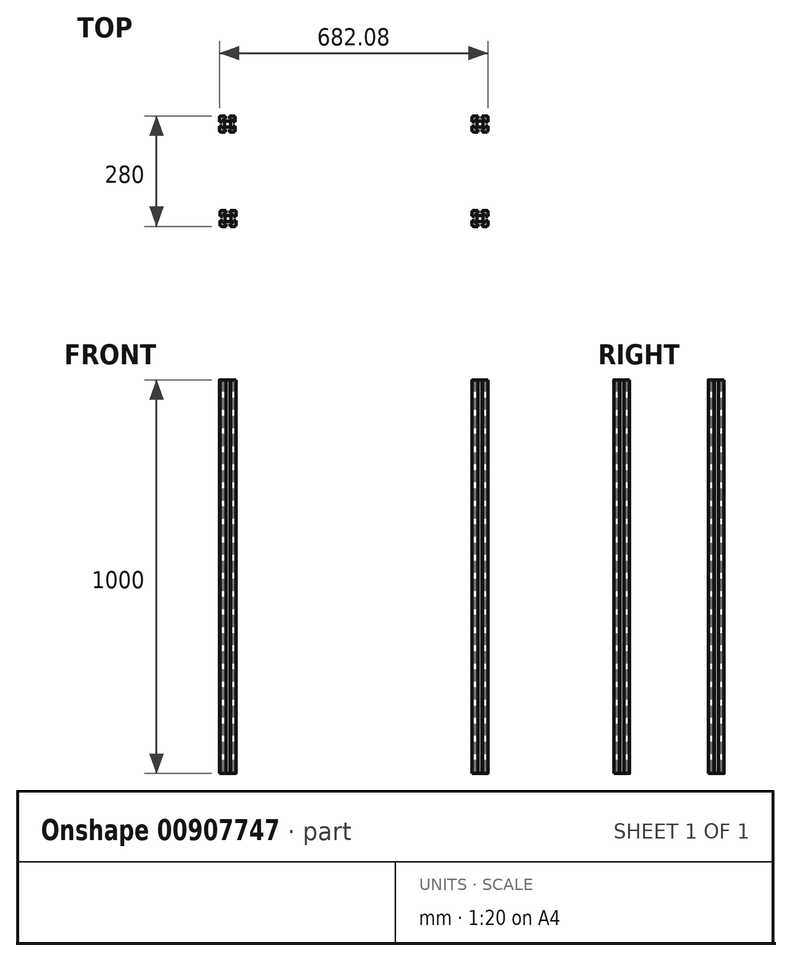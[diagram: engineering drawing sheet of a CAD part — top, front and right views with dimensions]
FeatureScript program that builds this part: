
annotation { "Feature Type Name" : "Feature", "Feature Type Description" : "" }
export const myFeature = defineFeature(function(context is Context, id is Id, definition is map)
    precondition{}
    {
        {
            var Q0;
            Q0=qCreatedBy(makeId("Top.planeOp"),FACE);
            var sketch = newSketch(context, id + "F0", { "sketchPlane" : qUnion([Q0])});
            skLineSegment(sketch, "E0", {"start": v(5.8, -18.5) * mm, "end": v(5.8, -20) * mm});
            skLineSegment(sketch, "E1", {"start": v(5.8, -20) * mm, "end": v(17, -20) * mm});
            skArc(sketch, "E2", {"start": v(17, -20) * mm, "mid": v(19.12, -19.12) * mm, "end": v(20, -17) * mm});
            skLineSegment(sketch, "E3", {"start": v(20, -17) * mm, "end": v(20, -5.8) * mm});
            skLineSegment(sketch, "E4", {"start": v(20, -5.8) * mm, "end": v(18.5, -5.8) * mm});
            skLineSegment(sketch, "E5", {"start": v(18.5, -5.8) * mm, "end": v(18.5, -5) * mm});
            skLineSegment(sketch, "E6", {"start": v(18.5, -5) * mm, "end": v(14, -5) * mm});
            skLineSegment(sketch, "E7", {"start": v(14, -5) * mm, "end": v(14, -10.05) * mm});
            skLineSegment(sketch, "E8", {"start": v(14, -10.05) * mm, "end": v(11.46, -10.05) * mm});
            skLineSegment(sketch, "E9", {"start": v(11.46, -10.05) * mm, "end": v(7.5, -6.09) * mm});
            skLineSegment(sketch, "E10", {"start": v(7.5, -6.09) * mm, "end": v(7.5, 6.09) * mm});
            skLineSegment(sketch, "E11", {"start": v(7.5, 6.09) * mm, "end": v(11.46, 10.05) * mm});
            skLineSegment(sketch, "E12", {"start": v(11.46, 10.05) * mm, "end": v(14, 10.05) * mm});
            skLineSegment(sketch, "E13", {"start": v(14, 10.05) * mm, "end": v(14, 5) * mm});
            skLineSegment(sketch, "E14", {"start": v(14, 5) * mm, "end": v(18.5, 5) * mm});
            skLineSegment(sketch, "E15", {"start": v(18.5, 5) * mm, "end": v(18.5, 5.8) * mm});
            skLineSegment(sketch, "E16", {"start": v(18.5, 5.8) * mm, "end": v(20, 5.8) * mm});
            skLineSegment(sketch, "E17", {"start": v(20, 5.8) * mm, "end": v(20, 17) * mm});
            skArc(sketch, "E18", {"start": v(20, 17) * mm, "mid": v(19.12, 19.12) * mm, "end": v(17, 20) * mm});
            skLineSegment(sketch, "E19", {"start": v(17, 20) * mm, "end": v(5.8, 20) * mm});
            skLineSegment(sketch, "E20", {"start": v(5.8, 20) * mm, "end": v(5.8, 18.5) * mm});
            skLineSegment(sketch, "E21", {"start": v(5.8, 18.5) * mm, "end": v(5, 18.5) * mm});
            skLineSegment(sketch, "E22", {"start": v(5, 18.5) * mm, "end": v(5, 14) * mm});
            skLineSegment(sketch, "E23", {"start": v(5, 14) * mm, "end": v(10.05, 14) * mm});
            skLineSegment(sketch, "E24", {"start": v(10.05, 14) * mm, "end": v(10.05, 11.46) * mm});
            skLineSegment(sketch, "E25", {"start": v(10.05, 11.46) * mm, "end": v(6.09, 7.5) * mm});
            skLineSegment(sketch, "E26", {"start": v(6.09, 7.5) * mm, "end": v(-6.09, 7.5) * mm});
            skLineSegment(sketch, "E27", {"start": v(-6.09, 7.5) * mm, "end": v(-10.05, 11.46) * mm});
            skLineSegment(sketch, "E28", {"start": v(-10.05, 11.46) * mm, "end": v(-10.05, 14) * mm});
            skLineSegment(sketch, "E29", {"start": v(-10.05, 14) * mm, "end": v(-5, 14) * mm});
            skLineSegment(sketch, "E30", {"start": v(-5, 14) * mm, "end": v(-5, 18.5) * mm});
            skLineSegment(sketch, "E31", {"start": v(-5, 18.5) * mm, "end": v(-5.8, 18.5) * mm});
            skLineSegment(sketch, "E32", {"start": v(-5.8, 18.5) * mm, "end": v(-5.8, 20) * mm});
            skLineSegment(sketch, "E33", {"start": v(-5.8, 20) * mm, "end": v(-17, 20) * mm});
            skArc(sketch, "E34", {"start": v(-17, 20) * mm, "mid": v(-19.12, 19.12) * mm, "end": v(-20, 17) * mm});
            skLineSegment(sketch, "E35", {"start": v(-20, 17) * mm, "end": v(-20, 5.8) * mm});
            skLineSegment(sketch, "E36", {"start": v(-20, 5.8) * mm, "end": v(-18.5, 5.8) * mm});
            skLineSegment(sketch, "E37", {"start": v(-18.5, 5.8) * mm, "end": v(-18.5, 5) * mm});
            skLineSegment(sketch, "E38", {"start": v(-18.5, 5) * mm, "end": v(-14, 5) * mm});
            skLineSegment(sketch, "E39", {"start": v(-14, 5) * mm, "end": v(-14, 10.05) * mm});
            skLineSegment(sketch, "E40", {"start": v(-14, 10.05) * mm, "end": v(-11.46, 10.05) * mm});
            skLineSegment(sketch, "E41", {"start": v(-11.46, 10.05) * mm, "end": v(-7.5, 6.09) * mm});
            skLineSegment(sketch, "E42", {"start": v(-7.5, 6.09) * mm, "end": v(-7.5, -6.09) * mm});
            skLineSegment(sketch, "E43", {"start": v(-7.5, -6.09) * mm, "end": v(-11.46, -10.05) * mm});
            skLineSegment(sketch, "E44", {"start": v(-11.46, -10.05) * mm, "end": v(-14, -10.05) * mm});
            skLineSegment(sketch, "E45", {"start": v(-14, -10.05) * mm, "end": v(-14, -5) * mm});
            skLineSegment(sketch, "E46", {"start": v(-14, -5) * mm, "end": v(-18.5, -5) * mm});
            skLineSegment(sketch, "E47", {"start": v(-18.5, -5) * mm, "end": v(-18.5, -5.8) * mm});
            skLineSegment(sketch, "E48", {"start": v(-18.5, -5.8) * mm, "end": v(-20, -5.8) * mm});
            skLineSegment(sketch, "E49", {"start": v(-20, -5.8) * mm, "end": v(-20, -17) * mm});
            skArc(sketch, "E50", {"start": v(-20, -17) * mm, "mid": v(-19.12, -19.12) * mm, "end": v(-17, -20) * mm});
            skLineSegment(sketch, "E51", {"start": v(-17, -20) * mm, "end": v(-5.8, -20) * mm});
            skLineSegment(sketch, "E52", {"start": v(-5.8, -20) * mm, "end": v(-5.8, -18.5) * mm});
            skLineSegment(sketch, "E53", {"start": v(-5.8, -18.5) * mm, "end": v(-5, -18.5) * mm});
            skLineSegment(sketch, "E54", {"start": v(-5, -18.5) * mm, "end": v(-5, -14) * mm});
            skLineSegment(sketch, "E55", {"start": v(-5, -14) * mm, "end": v(-10.05, -14) * mm});
            skLineSegment(sketch, "E56", {"start": v(-10.05, -14) * mm, "end": v(-10.05, -11.46) * mm});
            skLineSegment(sketch, "E57", {"start": v(-10.05, -11.46) * mm, "end": v(-6.09, -7.5) * mm});
            skLineSegment(sketch, "E58", {"start": v(-6.09, -7.5) * mm, "end": v(6.09, -7.5) * mm});
            skLineSegment(sketch, "E59", {"start": v(6.09, -7.5) * mm, "end": v(10.05, -11.46) * mm});
            skLineSegment(sketch, "E60", {"start": v(10.05, -11.46) * mm, "end": v(10.05, -14) * mm});
            skLineSegment(sketch, "E61", {"start": v(10.05, -14) * mm, "end": v(5, -14) * mm});
            skLineSegment(sketch, "E62", {"start": v(5, -14) * mm, "end": v(5, -18.5) * mm});
            skLineSegment(sketch, "E63", {"start": v(5, -18.5) * mm, "end": v(5.8, -18.5) * mm});
            skLineSegment(sketch, "E64", {"start": v(18.5, 9.5) * mm, "end": v(18.5, 14.5) * mm});
            skArc(sketch, "E65", {"start": v(15.5, 9.5) * mm, "mid": v(17, 8) * mm, "end": v(18.5, 9.5) * mm});
            skLineSegment(sketch, "E66", {"start": v(15.5, 11.75) * mm, "end": v(15.5, 9.5) * mm});
            skLineSegment(sketch, "E67", {"start": v(14.5, 11.75) * mm, "end": v(15.5, 11.75) * mm});
            skArc(sketch, "E68", {"start": v(11.75, 14.5) * mm, "mid": v(12.56, 12.56) * mm, "end": v(14.5, 11.75) * mm});
            skLineSegment(sketch, "E69", {"start": v(11.75, 15.5) * mm, "end": v(11.75, 14.5) * mm});
            skLineSegment(sketch, "E70", {"start": v(9.5, 15.5) * mm, "end": v(11.75, 15.5) * mm});
            skArc(sketch, "E71", {"start": v(9.5, 18.5) * mm, "mid": v(8, 17) * mm, "end": v(9.5, 15.5) * mm});
            skLineSegment(sketch, "E72", {"start": v(14.5, 18.5) * mm, "end": v(9.5, 18.5) * mm});
            skLineSegment(sketch, "E73", {"start": v(14.5, 17.25) * mm, "end": v(14.5, 18.5) * mm});
            skArc(sketch, "E74", {"start": v(17.25, 14.5) * mm, "mid": v(16.44, 16.44) * mm, "end": v(14.5, 17.25) * mm});
            skLineSegment(sketch, "E75", {"start": v(18.5, 14.5) * mm, "end": v(17.25, 14.5) * mm});
            skLineSegment(sketch, "E76", {"start": v(11.75, -14.5) * mm, "end": v(11.75, -15.5) * mm});
            skArc(sketch, "E77", {"start": v(14.5, -11.75) * mm, "mid": v(12.56, -12.56) * mm, "end": v(11.75, -14.5) * mm});
            skLineSegment(sketch, "E78", {"start": v(15.5, -11.75) * mm, "end": v(14.5, -11.75) * mm});
            skLineSegment(sketch, "E79", {"start": v(15.5, -9.5) * mm, "end": v(15.5, -11.75) * mm});
            skArc(sketch, "E80", {"start": v(18.5, -9.5) * mm, "mid": v(17, -8) * mm, "end": v(15.5, -9.5) * mm});
            skLineSegment(sketch, "E81", {"start": v(18.5, -14.5) * mm, "end": v(18.5, -9.5) * mm});
            skLineSegment(sketch, "E82", {"start": v(17.25, -14.5) * mm, "end": v(18.5, -14.5) * mm});
            skArc(sketch, "E83", {"start": v(14.5, -17.25) * mm, "mid": v(16.44, -16.44) * mm, "end": v(17.25, -14.5) * mm});
            skLineSegment(sketch, "E84", {"start": v(14.5, -18.5) * mm, "end": v(14.5, -17.25) * mm});
            skLineSegment(sketch, "E85", {"start": v(9.5, -18.5) * mm, "end": v(14.5, -18.5) * mm});
            skArc(sketch, "E86", {"start": v(9.5, -15.5) * mm, "mid": v(8, -17) * mm, "end": v(9.5, -18.5) * mm});
            skLineSegment(sketch, "E87", {"start": v(11.75, -15.5) * mm, "end": v(9.5, -15.5) * mm});
            skLineSegment(sketch, "E88", {"start": v(-2, 4.58) * mm, "end": v(-2.4, 5.5) * mm});
            skArc(sketch, "E89", {"start": v(2, 4.58) * mm, "mid": v(0, 5) * mm, "end": v(-2, 4.58) * mm});
            skLineSegment(sketch, "E90", {"start": v(2.4, 5.5) * mm, "end": v(2, 4.58) * mm});
            skLineSegment(sketch, "E91", {"start": v(5.5, 5.5) * mm, "end": v(2.4, 5.5) * mm});
            skLineSegment(sketch, "E92", {"start": v(5.5, 2.4) * mm, "end": v(5.5, 5.5) * mm});
            skLineSegment(sketch, "E93", {"start": v(4.58, 2) * mm, "end": v(5.5, 2.4) * mm});
            skArc(sketch, "E94", {"start": v(4.58, -2) * mm, "mid": v(5, 0) * mm, "end": v(4.58, 2) * mm});
            skLineSegment(sketch, "E95", {"start": v(5.5, -2.4) * mm, "end": v(4.58, -2) * mm});
            skLineSegment(sketch, "E96", {"start": v(5.5, -5.5) * mm, "end": v(5.5, -2.4) * mm});
            skLineSegment(sketch, "E97", {"start": v(2.4, -5.5) * mm, "end": v(5.5, -5.5) * mm});
            skLineSegment(sketch, "E98", {"start": v(2, -4.58) * mm, "end": v(2.4, -5.5) * mm});
            skArc(sketch, "E99", {"start": v(-2, -4.58) * mm, "mid": v(0, -5) * mm, "end": v(2, -4.58) * mm});
            skLineSegment(sketch, "E100", {"start": v(-2.4, -5.5) * mm, "end": v(-2, -4.58) * mm});
            skLineSegment(sketch, "E101", {"start": v(-5.5, -5.5) * mm, "end": v(-2.4, -5.5) * mm});
            skLineSegment(sketch, "E102", {"start": v(-5.5, -2.4) * mm, "end": v(-5.5, -5.5) * mm});
            skLineSegment(sketch, "E103", {"start": v(-4.58, -2) * mm, "end": v(-5.5, -2.4) * mm});
            skArc(sketch, "E104", {"start": v(-4.58, 2) * mm, "mid": v(-5, 0) * mm, "end": v(-4.58, -2) * mm});
            skLineSegment(sketch, "E105", {"start": v(-5.5, 2.4) * mm, "end": v(-4.58, 2) * mm});
            skLineSegment(sketch, "E106", {"start": v(-5.5, 5.5) * mm, "end": v(-5.5, 2.4) * mm});
            skLineSegment(sketch, "E107", {"start": v(-2.4, 5.5) * mm, "end": v(-5.5, 5.5) * mm});
            skLineSegment(sketch, "E108", {"start": v(-18.5, -9.5) * mm, "end": v(-18.5, -14.5) * mm});
            skArc(sketch, "E109", {"start": v(-15.5, -9.5) * mm, "mid": v(-17, -8) * mm, "end": v(-18.5, -9.5) * mm});
            skLineSegment(sketch, "E110", {"start": v(-15.5, -11.75) * mm, "end": v(-15.5, -9.5) * mm});
            skLineSegment(sketch, "E111", {"start": v(-14.5, -11.75) * mm, "end": v(-15.5, -11.75) * mm});
            skArc(sketch, "E112", {"start": v(-11.75, -14.5) * mm, "mid": v(-12.56, -12.56) * mm, "end": v(-14.5, -11.75) * mm});
            skLineSegment(sketch, "E113", {"start": v(-11.75, -15.5) * mm, "end": v(-11.75, -14.5) * mm});
            skLineSegment(sketch, "E114", {"start": v(-9.5, -15.5) * mm, "end": v(-11.75, -15.5) * mm});
            skArc(sketch, "E115", {"start": v(-9.5, -18.5) * mm, "mid": v(-8, -17) * mm, "end": v(-9.5, -15.5) * mm});
            skLineSegment(sketch, "E116", {"start": v(-14.5, -18.5) * mm, "end": v(-9.5, -18.5) * mm});
            skLineSegment(sketch, "E117", {"start": v(-14.5, -17.25) * mm, "end": v(-14.5, -18.5) * mm});
            skArc(sketch, "E118", {"start": v(-17.25, -14.5) * mm, "mid": v(-16.44, -16.44) * mm, "end": v(-14.5, -17.25) * mm});
            skLineSegment(sketch, "E119", {"start": v(-18.5, -14.5) * mm, "end": v(-17.25, -14.5) * mm});
            skLineSegment(sketch, "E120", {"start": v(-11.75, 14.5) * mm, "end": v(-11.75, 15.5) * mm});
            skArc(sketch, "E121", {"start": v(-14.5, 11.75) * mm, "mid": v(-12.56, 12.56) * mm, "end": v(-11.75, 14.5) * mm});
            skLineSegment(sketch, "E122", {"start": v(-15.5, 11.75) * mm, "end": v(-14.5, 11.75) * mm});
            skLineSegment(sketch, "E123", {"start": v(-15.5, 9.5) * mm, "end": v(-15.5, 11.75) * mm});
            skArc(sketch, "E124", {"start": v(-18.5, 9.5) * mm, "mid": v(-17, 8) * mm, "end": v(-15.5, 9.5) * mm});
            skLineSegment(sketch, "E125", {"start": v(-18.5, 14.5) * mm, "end": v(-18.5, 9.5) * mm});
            skLineSegment(sketch, "E126", {"start": v(-17.25, 14.5) * mm, "end": v(-18.5, 14.5) * mm});
            skArc(sketch, "E127", {"start": v(-14.5, 17.25) * mm, "mid": v(-16.44, 16.44) * mm, "end": v(-17.25, 14.5) * mm});
            skLineSegment(sketch, "E128", {"start": v(-14.5, 18.5) * mm, "end": v(-14.5, 17.25) * mm});
            skLineSegment(sketch, "E129", {"start": v(-9.5, 18.5) * mm, "end": v(-14.5, 18.5) * mm});
            skArc(sketch, "E130", {"start": v(-9.5, 15.5) * mm, "mid": v(-8, 17) * mm, "end": v(-9.5, 18.5) * mm});
            skLineSegment(sketch, "E131", {"start": v(-11.75, 15.5) * mm, "end": v(-9.5, 15.5) * mm});
            skLineSegment(sketch, "E132", {"start": v(645.88, -18.5) * mm, "end": v(645.88, -20) * mm});
            skLineSegment(sketch, "E133", {"start": v(645.88, -20) * mm, "end": v(657.08, -20) * mm});
            skArc(sketch, "E134", {"start": v(657.08, -20) * mm, "mid": v(659.2, -19.12) * mm, "end": v(660.08, -17) * mm});
            skLineSegment(sketch, "E135", {"start": v(660.08, -17) * mm, "end": v(660.08, -5.8) * mm});
            skLineSegment(sketch, "E136", {"start": v(660.08, -5.8) * mm, "end": v(658.58, -5.8) * mm});
            skLineSegment(sketch, "E137", {"start": v(658.58, -5.8) * mm, "end": v(658.58, -5) * mm});
            skLineSegment(sketch, "E138", {"start": v(658.58, -5) * mm, "end": v(654.08, -5) * mm});
            skLineSegment(sketch, "E139", {"start": v(654.08, -5) * mm, "end": v(654.08, -10.05) * mm});
            skLineSegment(sketch, "E140", {"start": v(654.08, -10.05) * mm, "end": v(651.54, -10.05) * mm});
            skLineSegment(sketch, "E141", {"start": v(651.54, -10.05) * mm, "end": v(647.58, -6.09) * mm});
            skLineSegment(sketch, "E142", {"start": v(647.58, -6.09) * mm, "end": v(647.58, 6.09) * mm});
            skLineSegment(sketch, "E143", {"start": v(647.58, 6.09) * mm, "end": v(651.54, 10.05) * mm});
            skLineSegment(sketch, "E144", {"start": v(651.54, 10.05) * mm, "end": v(654.08, 10.05) * mm});
            skLineSegment(sketch, "E145", {"start": v(654.08, 10.05) * mm, "end": v(654.08, 5) * mm});
            skLineSegment(sketch, "E146", {"start": v(654.08, 5) * mm, "end": v(658.58, 5) * mm});
            skLineSegment(sketch, "E147", {"start": v(658.58, 5) * mm, "end": v(658.58, 5.8) * mm});
            skLineSegment(sketch, "E148", {"start": v(658.58, 5.8) * mm, "end": v(660.08, 5.8) * mm});
            skLineSegment(sketch, "E149", {"start": v(660.08, 5.8) * mm, "end": v(660.08, 17) * mm});
            skArc(sketch, "E150", {"start": v(660.08, 17) * mm, "mid": v(659.2, 19.12) * mm, "end": v(657.08, 20) * mm});
            skLineSegment(sketch, "E151", {"start": v(657.08, 20) * mm, "end": v(645.88, 20) * mm});
            skLineSegment(sketch, "E152", {"start": v(645.88, 20) * mm, "end": v(645.88, 18.5) * mm});
            skLineSegment(sketch, "E153", {"start": v(645.88, 18.5) * mm, "end": v(645.08, 18.5) * mm});
            skLineSegment(sketch, "E154", {"start": v(645.08, 18.5) * mm, "end": v(645.08, 14) * mm});
            skLineSegment(sketch, "E155", {"start": v(645.08, 14) * mm, "end": v(650.13, 14) * mm});
            skLineSegment(sketch, "E156", {"start": v(650.13, 14) * mm, "end": v(650.13, 11.46) * mm});
            skLineSegment(sketch, "E157", {"start": v(650.13, 11.46) * mm, "end": v(646.16, 7.5) * mm});
            skLineSegment(sketch, "E158", {"start": v(646.16, 7.5) * mm, "end": v(634, 7.5) * mm});
            skLineSegment(sketch, "E159", {"start": v(634, 7.5) * mm, "end": v(630.03, 11.46) * mm});
            skLineSegment(sketch, "E160", {"start": v(630.03, 11.46) * mm, "end": v(630.03, 14) * mm});
            skLineSegment(sketch, "E161", {"start": v(630.03, 14) * mm, "end": v(635.08, 14) * mm});
            skLineSegment(sketch, "E162", {"start": v(635.08, 14) * mm, "end": v(635.08, 18.5) * mm});
            skLineSegment(sketch, "E163", {"start": v(635.08, 18.5) * mm, "end": v(634.28, 18.5) * mm});
            skLineSegment(sketch, "E164", {"start": v(634.28, 18.5) * mm, "end": v(634.28, 20) * mm});
            skLineSegment(sketch, "E165", {"start": v(634.28, 20) * mm, "end": v(623.08, 20) * mm});
            skArc(sketch, "E166", {"start": v(623.08, 20) * mm, "mid": v(620.96, 19.12) * mm, "end": v(620.08, 17) * mm});
            skLineSegment(sketch, "E167", {"start": v(620.08, 17) * mm, "end": v(620.08, 5.8) * mm});
            skLineSegment(sketch, "E168", {"start": v(620.08, 5.8) * mm, "end": v(621.58, 5.8) * mm});
            skLineSegment(sketch, "E169", {"start": v(621.58, 5.8) * mm, "end": v(621.58, 5) * mm});
            skLineSegment(sketch, "E170", {"start": v(621.58, 5) * mm, "end": v(626.08, 5) * mm});
            skLineSegment(sketch, "E171", {"start": v(626.08, 5) * mm, "end": v(626.08, 10.05) * mm});
            skLineSegment(sketch, "E172", {"start": v(626.08, 10.05) * mm, "end": v(628.61, 10.05) * mm});
            skLineSegment(sketch, "E173", {"start": v(628.61, 10.05) * mm, "end": v(632.58, 6.09) * mm});
            skLineSegment(sketch, "E174", {"start": v(632.58, 6.09) * mm, "end": v(632.58, -6.09) * mm});
            skLineSegment(sketch, "E175", {"start": v(632.58, -6.09) * mm, "end": v(628.61, -10.05) * mm});
            skLineSegment(sketch, "E176", {"start": v(628.61, -10.05) * mm, "end": v(626.08, -10.05) * mm});
            skLineSegment(sketch, "E177", {"start": v(626.08, -10.05) * mm, "end": v(626.08, -5) * mm});
            skLineSegment(sketch, "E178", {"start": v(626.08, -5) * mm, "end": v(621.58, -5) * mm});
            skLineSegment(sketch, "E179", {"start": v(621.58, -5) * mm, "end": v(621.58, -5.8) * mm});
            skLineSegment(sketch, "E180", {"start": v(621.58, -5.8) * mm, "end": v(620.08, -5.8) * mm});
            skLineSegment(sketch, "E181", {"start": v(620.08, -5.8) * mm, "end": v(620.08, -17) * mm});
            skArc(sketch, "E182", {"start": v(620.08, -17) * mm, "mid": v(620.96, -19.12) * mm, "end": v(623.08, -20) * mm});
            skLineSegment(sketch, "E183", {"start": v(623.08, -20) * mm, "end": v(634.28, -20) * mm});
            skLineSegment(sketch, "E184", {"start": v(634.28, -20) * mm, "end": v(634.28, -18.5) * mm});
            skLineSegment(sketch, "E185", {"start": v(634.28, -18.5) * mm, "end": v(635.08, -18.5) * mm});
            skLineSegment(sketch, "E186", {"start": v(635.08, -18.5) * mm, "end": v(635.08, -14) * mm});
            skLineSegment(sketch, "E187", {"start": v(635.08, -14) * mm, "end": v(630.03, -14) * mm});
            skLineSegment(sketch, "E188", {"start": v(630.03, -14) * mm, "end": v(630.03, -11.46) * mm});
            skLineSegment(sketch, "E189", {"start": v(630.03, -11.46) * mm, "end": v(634, -7.5) * mm});
            skLineSegment(sketch, "E190", {"start": v(634, -7.5) * mm, "end": v(646.16, -7.5) * mm});
            skLineSegment(sketch, "E191", {"start": v(646.16, -7.5) * mm, "end": v(650.13, -11.46) * mm});
            skLineSegment(sketch, "E192", {"start": v(650.13, -11.46) * mm, "end": v(650.13, -14) * mm});
            skLineSegment(sketch, "E193", {"start": v(650.13, -14) * mm, "end": v(645.08, -14) * mm});
            skLineSegment(sketch, "E194", {"start": v(645.08, -14) * mm, "end": v(645.08, -18.5) * mm});
            skLineSegment(sketch, "E195", {"start": v(645.08, -18.5) * mm, "end": v(645.88, -18.5) * mm});
            skLineSegment(sketch, "E196", {"start": v(658.58, 9.5) * mm, "end": v(658.58, 14.5) * mm});
            skArc(sketch, "E197", {"start": v(655.58, 9.5) * mm, "mid": v(657.08, 8) * mm, "end": v(658.58, 9.5) * mm});
            skLineSegment(sketch, "E198", {"start": v(655.58, 11.75) * mm, "end": v(655.58, 9.5) * mm});
            skLineSegment(sketch, "E199", {"start": v(654.58, 11.75) * mm, "end": v(655.58, 11.75) * mm});
            skArc(sketch, "E200", {"start": v(651.83, 14.5) * mm, "mid": v(652.63, 12.56) * mm, "end": v(654.58, 11.75) * mm});
            skLineSegment(sketch, "E201", {"start": v(651.83, 15.5) * mm, "end": v(651.83, 14.5) * mm});
            skLineSegment(sketch, "E202", {"start": v(649.58, 15.5) * mm, "end": v(651.83, 15.5) * mm});
            skArc(sketch, "E203", {"start": v(649.58, 18.5) * mm, "mid": v(648.08, 17) * mm, "end": v(649.58, 15.5) * mm});
            skLineSegment(sketch, "E204", {"start": v(654.58, 18.5) * mm, "end": v(649.58, 18.5) * mm});
            skLineSegment(sketch, "E205", {"start": v(654.58, 17.25) * mm, "end": v(654.58, 18.5) * mm});
            skArc(sketch, "E206", {"start": v(657.33, 14.5) * mm, "mid": v(656.52, 16.44) * mm, "end": v(654.58, 17.25) * mm});
            skLineSegment(sketch, "E207", {"start": v(658.58, 14.5) * mm, "end": v(657.33, 14.5) * mm});
            skLineSegment(sketch, "E208", {"start": v(651.83, -14.5) * mm, "end": v(651.83, -15.5) * mm});
            skArc(sketch, "E209", {"start": v(654.58, -11.75) * mm, "mid": v(652.63, -12.56) * mm, "end": v(651.83, -14.5) * mm});
            skLineSegment(sketch, "E210", {"start": v(655.58, -11.75) * mm, "end": v(654.58, -11.75) * mm});
            skLineSegment(sketch, "E211", {"start": v(655.58, -9.5) * mm, "end": v(655.58, -11.75) * mm});
            skArc(sketch, "E212", {"start": v(658.58, -9.5) * mm, "mid": v(657.08, -8) * mm, "end": v(655.58, -9.5) * mm});
            skLineSegment(sketch, "E213", {"start": v(658.58, -14.5) * mm, "end": v(658.58, -9.5) * mm});
            skLineSegment(sketch, "E214", {"start": v(657.33, -14.5) * mm, "end": v(658.58, -14.5) * mm});
            skArc(sketch, "E215", {"start": v(654.58, -17.25) * mm, "mid": v(656.52, -16.44) * mm, "end": v(657.33, -14.5) * mm});
            skLineSegment(sketch, "E216", {"start": v(654.58, -18.5) * mm, "end": v(654.58, -17.25) * mm});
            skLineSegment(sketch, "E217", {"start": v(649.58, -18.5) * mm, "end": v(654.58, -18.5) * mm});
            skArc(sketch, "E218", {"start": v(649.58, -15.5) * mm, "mid": v(648.08, -17) * mm, "end": v(649.58, -18.5) * mm});
            skLineSegment(sketch, "E219", {"start": v(651.83, -15.5) * mm, "end": v(649.58, -15.5) * mm});
            skLineSegment(sketch, "E220", {"start": v(638.08, 4.58) * mm, "end": v(637.68, 5.5) * mm});
            skArc(sketch, "E221", {"start": v(642.08, 4.58) * mm, "mid": v(640.08, 5) * mm, "end": v(638.08, 4.58) * mm});
            skLineSegment(sketch, "E222", {"start": v(642.47, 5.5) * mm, "end": v(642.08, 4.58) * mm});
            skLineSegment(sketch, "E223", {"start": v(645.58, 5.5) * mm, "end": v(642.47, 5.5) * mm});
            skLineSegment(sketch, "E224", {"start": v(645.58, 2.4) * mm, "end": v(645.58, 5.5) * mm});
            skLineSegment(sketch, "E225", {"start": v(644.66, 2) * mm, "end": v(645.58, 2.4) * mm});
            skArc(sketch, "E226", {"start": v(644.66, -2) * mm, "mid": v(645.08, 0) * mm, "end": v(644.66, 2) * mm});
            skLineSegment(sketch, "E227", {"start": v(645.58, -2.4) * mm, "end": v(644.66, -2) * mm});
            skLineSegment(sketch, "E228", {"start": v(645.58, -5.5) * mm, "end": v(645.58, -2.4) * mm});
            skLineSegment(sketch, "E229", {"start": v(642.47, -5.5) * mm, "end": v(645.58, -5.5) * mm});
            skLineSegment(sketch, "E230", {"start": v(642.08, -4.58) * mm, "end": v(642.47, -5.5) * mm});
            skArc(sketch, "E231", {"start": v(638.08, -4.58) * mm, "mid": v(640.08, -5) * mm, "end": v(642.08, -4.58) * mm});
            skLineSegment(sketch, "E232", {"start": v(637.68, -5.5) * mm, "end": v(638.08, -4.58) * mm});
            skLineSegment(sketch, "E233", {"start": v(634.58, -5.5) * mm, "end": v(637.68, -5.5) * mm});
            skLineSegment(sketch, "E234", {"start": v(634.58, -2.4) * mm, "end": v(634.58, -5.5) * mm});
            skLineSegment(sketch, "E235", {"start": v(635.5, -2) * mm, "end": v(634.58, -2.4) * mm});
            skArc(sketch, "E236", {"start": v(635.5, 2) * mm, "mid": v(635.08, 0) * mm, "end": v(635.5, -2) * mm});
            skLineSegment(sketch, "E237", {"start": v(634.58, 2.4) * mm, "end": v(635.5, 2) * mm});
            skLineSegment(sketch, "E238", {"start": v(634.58, 5.5) * mm, "end": v(634.58, 2.4) * mm});
            skLineSegment(sketch, "E239", {"start": v(637.68, 5.5) * mm, "end": v(634.58, 5.5) * mm});
            skLineSegment(sketch, "E240", {"start": v(621.58, -9.5) * mm, "end": v(621.58, -14.5) * mm});
            skArc(sketch, "E241", {"start": v(624.58, -9.5) * mm, "mid": v(623.08, -8) * mm, "end": v(621.58, -9.5) * mm});
            skLineSegment(sketch, "E242", {"start": v(624.58, -11.75) * mm, "end": v(624.58, -9.5) * mm});
            skLineSegment(sketch, "E243", {"start": v(625.58, -11.75) * mm, "end": v(624.58, -11.75) * mm});
            skArc(sketch, "E244", {"start": v(628.33, -14.5) * mm, "mid": v(627.52, -12.56) * mm, "end": v(625.58, -11.75) * mm});
            skLineSegment(sketch, "E245", {"start": v(628.33, -15.5) * mm, "end": v(628.33, -14.5) * mm});
            skLineSegment(sketch, "E246", {"start": v(630.58, -15.5) * mm, "end": v(628.33, -15.5) * mm});
            skArc(sketch, "E247", {"start": v(630.58, -18.5) * mm, "mid": v(632.08, -17) * mm, "end": v(630.58, -15.5) * mm});
            skLineSegment(sketch, "E248", {"start": v(625.58, -18.5) * mm, "end": v(630.58, -18.5) * mm});
            skLineSegment(sketch, "E249", {"start": v(625.58, -17.25) * mm, "end": v(625.58, -18.5) * mm});
            skArc(sketch, "E250", {"start": v(622.83, -14.5) * mm, "mid": v(623.63, -16.44) * mm, "end": v(625.58, -17.25) * mm});
            skLineSegment(sketch, "E251", {"start": v(621.58, -14.5) * mm, "end": v(622.83, -14.5) * mm});
            skLineSegment(sketch, "E252", {"start": v(628.33, 14.5) * mm, "end": v(628.33, 15.5) * mm});
            skArc(sketch, "E253", {"start": v(625.58, 11.75) * mm, "mid": v(627.52, 12.56) * mm, "end": v(628.33, 14.5) * mm});
            skLineSegment(sketch, "E254", {"start": v(624.58, 11.75) * mm, "end": v(625.58, 11.75) * mm});
            skLineSegment(sketch, "E255", {"start": v(624.58, 9.5) * mm, "end": v(624.58, 11.75) * mm});
            skArc(sketch, "E256", {"start": v(621.58, 9.5) * mm, "mid": v(623.08, 8) * mm, "end": v(624.58, 9.5) * mm});
            skLineSegment(sketch, "E257", {"start": v(621.58, 14.5) * mm, "end": v(621.58, 9.5) * mm});
            skLineSegment(sketch, "E258", {"start": v(622.83, 14.5) * mm, "end": v(621.58, 14.5) * mm});
            skArc(sketch, "E259", {"start": v(625.58, 17.25) * mm, "mid": v(623.63, 16.44) * mm, "end": v(622.83, 14.5) * mm});
            skLineSegment(sketch, "E260", {"start": v(625.58, 18.5) * mm, "end": v(625.58, 17.25) * mm});
            skLineSegment(sketch, "E261", {"start": v(630.58, 18.5) * mm, "end": v(625.58, 18.5) * mm});
            skArc(sketch, "E262", {"start": v(630.58, 15.5) * mm, "mid": v(632.08, 17) * mm, "end": v(630.58, 18.5) * mm});
            skLineSegment(sketch, "E263", {"start": v(628.33, 15.5) * mm, "end": v(630.58, 15.5) * mm});
            skLineSegment(sketch, "E264", {"start": v(645.88, 221.5) * mm, "end": v(645.88, 220) * mm});
            skLineSegment(sketch, "E265", {"start": v(645.88, 220) * mm, "end": v(657.08, 220) * mm});
            skArc(sketch, "E266", {"start": v(657.08, 220) * mm, "mid": v(659.2, 220.88) * mm, "end": v(660.08, 223) * mm});
            skLineSegment(sketch, "E267", {"start": v(660.08, 223) * mm, "end": v(660.08, 234.2) * mm});
            skLineSegment(sketch, "E268", {"start": v(660.08, 234.2) * mm, "end": v(658.58, 234.2) * mm});
            skLineSegment(sketch, "E269", {"start": v(658.58, 234.2) * mm, "end": v(658.58, 235) * mm});
            skLineSegment(sketch, "E270", {"start": v(658.58, 235) * mm, "end": v(654.08, 235) * mm});
            skLineSegment(sketch, "E271", {"start": v(654.08, 235) * mm, "end": v(654.08, 229.95) * mm});
            skLineSegment(sketch, "E272", {"start": v(654.08, 229.95) * mm, "end": v(651.54, 229.95) * mm});
            skLineSegment(sketch, "E273", {"start": v(651.54, 229.95) * mm, "end": v(647.58, 233.91) * mm});
            skLineSegment(sketch, "E274", {"start": v(647.58, 233.91) * mm, "end": v(647.58, 246.09) * mm});
            skLineSegment(sketch, "E275", {"start": v(647.58, 246.09) * mm, "end": v(651.54, 250.05) * mm});
            skLineSegment(sketch, "E276", {"start": v(651.54, 250.05) * mm, "end": v(654.08, 250.05) * mm});
            skLineSegment(sketch, "E277", {"start": v(654.08, 250.05) * mm, "end": v(654.08, 245) * mm});
            skLineSegment(sketch, "E278", {"start": v(654.08, 245) * mm, "end": v(658.58, 245) * mm});
            skLineSegment(sketch, "E279", {"start": v(658.58, 245) * mm, "end": v(658.58, 245.8) * mm});
            skLineSegment(sketch, "E280", {"start": v(658.58, 245.8) * mm, "end": v(660.08, 245.8) * mm});
            skLineSegment(sketch, "E281", {"start": v(660.08, 245.8) * mm, "end": v(660.08, 257) * mm});
            skArc(sketch, "E282", {"start": v(660.08, 257) * mm, "mid": v(659.2, 259.12) * mm, "end": v(657.08, 260) * mm});
            skLineSegment(sketch, "E283", {"start": v(657.08, 260) * mm, "end": v(645.88, 260) * mm});
            skLineSegment(sketch, "E284", {"start": v(645.88, 260) * mm, "end": v(645.88, 258.5) * mm});
            skLineSegment(sketch, "E285", {"start": v(645.88, 258.5) * mm, "end": v(645.08, 258.5) * mm});
            skLineSegment(sketch, "E286", {"start": v(645.08, 258.5) * mm, "end": v(645.08, 254) * mm});
            skLineSegment(sketch, "E287", {"start": v(645.08, 254) * mm, "end": v(650.13, 254) * mm});
            skLineSegment(sketch, "E288", {"start": v(650.13, 254) * mm, "end": v(650.13, 251.46) * mm});
            skLineSegment(sketch, "E289", {"start": v(650.13, 251.46) * mm, "end": v(646.16, 247.5) * mm});
            skLineSegment(sketch, "E290", {"start": v(646.16, 247.5) * mm, "end": v(634, 247.5) * mm});
            skLineSegment(sketch, "E291", {"start": v(634, 247.5) * mm, "end": v(630.03, 251.46) * mm});
            skLineSegment(sketch, "E292", {"start": v(630.03, 251.46) * mm, "end": v(630.03, 254) * mm});
            skLineSegment(sketch, "E293", {"start": v(630.03, 254) * mm, "end": v(635.08, 254) * mm});
            skLineSegment(sketch, "E294", {"start": v(635.08, 254) * mm, "end": v(635.08, 258.5) * mm});
            skLineSegment(sketch, "E295", {"start": v(635.08, 258.5) * mm, "end": v(634.28, 258.5) * mm});
            skLineSegment(sketch, "E296", {"start": v(634.28, 258.5) * mm, "end": v(634.28, 260) * mm});
            skLineSegment(sketch, "E297", {"start": v(634.28, 260) * mm, "end": v(623.08, 260) * mm});
            skArc(sketch, "E298", {"start": v(623.08, 260) * mm, "mid": v(620.96, 259.12) * mm, "end": v(620.08, 257) * mm});
            skLineSegment(sketch, "E299", {"start": v(620.08, 257) * mm, "end": v(620.08, 245.8) * mm});
            skLineSegment(sketch, "E300", {"start": v(620.08, 245.8) * mm, "end": v(621.58, 245.8) * mm});
            skLineSegment(sketch, "E301", {"start": v(621.58, 245.8) * mm, "end": v(621.58, 245) * mm});
            skLineSegment(sketch, "E302", {"start": v(621.58, 245) * mm, "end": v(626.08, 245) * mm});
            skLineSegment(sketch, "E303", {"start": v(626.08, 245) * mm, "end": v(626.08, 250.05) * mm});
            skLineSegment(sketch, "E304", {"start": v(626.08, 250.05) * mm, "end": v(628.61, 250.05) * mm});
            skLineSegment(sketch, "E305", {"start": v(628.61, 250.05) * mm, "end": v(632.58, 246.09) * mm});
            skLineSegment(sketch, "E306", {"start": v(632.58, 246.09) * mm, "end": v(632.58, 233.91) * mm});
            skLineSegment(sketch, "E307", {"start": v(632.58, 233.91) * mm, "end": v(628.61, 229.95) * mm});
            skLineSegment(sketch, "E308", {"start": v(628.61, 229.95) * mm, "end": v(626.08, 229.95) * mm});
            skLineSegment(sketch, "E309", {"start": v(626.08, 229.95) * mm, "end": v(626.08, 235) * mm});
            skLineSegment(sketch, "E310", {"start": v(626.08, 235) * mm, "end": v(621.58, 235) * mm});
            skLineSegment(sketch, "E311", {"start": v(621.58, 235) * mm, "end": v(621.58, 234.2) * mm});
            skLineSegment(sketch, "E312", {"start": v(621.58, 234.2) * mm, "end": v(620.08, 234.2) * mm});
            skLineSegment(sketch, "E313", {"start": v(620.08, 234.2) * mm, "end": v(620.08, 223) * mm});
            skArc(sketch, "E314", {"start": v(620.08, 223) * mm, "mid": v(620.96, 220.88) * mm, "end": v(623.08, 220) * mm});
            skLineSegment(sketch, "E315", {"start": v(623.08, 220) * mm, "end": v(634.28, 220) * mm});
            skLineSegment(sketch, "E316", {"start": v(634.28, 220) * mm, "end": v(634.28, 221.5) * mm});
            skLineSegment(sketch, "E317", {"start": v(634.28, 221.5) * mm, "end": v(635.08, 221.5) * mm});
            skLineSegment(sketch, "E318", {"start": v(635.08, 221.5) * mm, "end": v(635.08, 226) * mm});
            skLineSegment(sketch, "E319", {"start": v(635.08, 226) * mm, "end": v(630.03, 226) * mm});
            skLineSegment(sketch, "E320", {"start": v(630.03, 226) * mm, "end": v(630.03, 228.54) * mm});
            skLineSegment(sketch, "E321", {"start": v(630.03, 228.54) * mm, "end": v(634, 232.5) * mm});
            skLineSegment(sketch, "E322", {"start": v(634, 232.5) * mm, "end": v(646.16, 232.5) * mm});
            skLineSegment(sketch, "E323", {"start": v(646.16, 232.5) * mm, "end": v(650.13, 228.54) * mm});
            skLineSegment(sketch, "E324", {"start": v(650.13, 228.54) * mm, "end": v(650.13, 226) * mm});
            skLineSegment(sketch, "E325", {"start": v(650.13, 226) * mm, "end": v(645.08, 226) * mm});
            skLineSegment(sketch, "E326", {"start": v(645.08, 226) * mm, "end": v(645.08, 221.5) * mm});
            skLineSegment(sketch, "E327", {"start": v(645.08, 221.5) * mm, "end": v(645.88, 221.5) * mm});
            skLineSegment(sketch, "E328", {"start": v(658.58, 249.5) * mm, "end": v(658.58, 254.5) * mm});
            skArc(sketch, "E329", {"start": v(655.58, 249.5) * mm, "mid": v(657.08, 248) * mm, "end": v(658.58, 249.5) * mm});
            skLineSegment(sketch, "E330", {"start": v(655.58, 251.75) * mm, "end": v(655.58, 249.5) * mm});
            skLineSegment(sketch, "E331", {"start": v(654.58, 251.75) * mm, "end": v(655.58, 251.75) * mm});
            skArc(sketch, "E332", {"start": v(651.83, 254.5) * mm, "mid": v(652.63, 252.56) * mm, "end": v(654.58, 251.75) * mm});
            skLineSegment(sketch, "E333", {"start": v(651.83, 255.5) * mm, "end": v(651.83, 254.5) * mm});
            skLineSegment(sketch, "E334", {"start": v(649.58, 255.5) * mm, "end": v(651.83, 255.5) * mm});
            skArc(sketch, "E335", {"start": v(649.58, 258.5) * mm, "mid": v(648.08, 257) * mm, "end": v(649.58, 255.5) * mm});
            skLineSegment(sketch, "E336", {"start": v(654.58, 258.5) * mm, "end": v(649.58, 258.5) * mm});
            skLineSegment(sketch, "E337", {"start": v(654.58, 257.25) * mm, "end": v(654.58, 258.5) * mm});
            skArc(sketch, "E338", {"start": v(657.33, 254.5) * mm, "mid": v(656.52, 256.44) * mm, "end": v(654.58, 257.25) * mm});
            skLineSegment(sketch, "E339", {"start": v(658.58, 254.5) * mm, "end": v(657.33, 254.5) * mm});
            skLineSegment(sketch, "E340", {"start": v(651.83, 225.5) * mm, "end": v(651.83, 224.5) * mm});
            skArc(sketch, "E341", {"start": v(654.58, 228.25) * mm, "mid": v(652.63, 227.44) * mm, "end": v(651.83, 225.5) * mm});
            skLineSegment(sketch, "E342", {"start": v(655.58, 228.25) * mm, "end": v(654.58, 228.25) * mm});
            skLineSegment(sketch, "E343", {"start": v(655.58, 230.5) * mm, "end": v(655.58, 228.25) * mm});
            skArc(sketch, "E344", {"start": v(658.58, 230.5) * mm, "mid": v(657.08, 232) * mm, "end": v(655.58, 230.5) * mm});
            skLineSegment(sketch, "E345", {"start": v(658.58, 225.5) * mm, "end": v(658.58, 230.5) * mm});
            skLineSegment(sketch, "E346", {"start": v(657.33, 225.5) * mm, "end": v(658.58, 225.5) * mm});
            skArc(sketch, "E347", {"start": v(654.58, 222.75) * mm, "mid": v(656.52, 223.56) * mm, "end": v(657.33, 225.5) * mm});
            skLineSegment(sketch, "E348", {"start": v(654.58, 221.5) * mm, "end": v(654.58, 222.75) * mm});
            skLineSegment(sketch, "E349", {"start": v(649.58, 221.5) * mm, "end": v(654.58, 221.5) * mm});
            skArc(sketch, "E350", {"start": v(649.58, 224.5) * mm, "mid": v(648.08, 223) * mm, "end": v(649.58, 221.5) * mm});
            skLineSegment(sketch, "E351", {"start": v(651.83, 224.5) * mm, "end": v(649.58, 224.5) * mm});
            skLineSegment(sketch, "E352", {"start": v(638.08, 244.58) * mm, "end": v(637.68, 245.5) * mm});
            skArc(sketch, "E353", {"start": v(642.08, 244.58) * mm, "mid": v(640.08, 245) * mm, "end": v(638.08, 244.58) * mm});
            skLineSegment(sketch, "E354", {"start": v(642.47, 245.5) * mm, "end": v(642.08, 244.58) * mm});
            skLineSegment(sketch, "E355", {"start": v(645.58, 245.5) * mm, "end": v(642.47, 245.5) * mm});
            skLineSegment(sketch, "E356", {"start": v(645.58, 242.4) * mm, "end": v(645.58, 245.5) * mm});
            skLineSegment(sketch, "E357", {"start": v(644.66, 242) * mm, "end": v(645.58, 242.4) * mm});
            skArc(sketch, "E358", {"start": v(644.66, 238) * mm, "mid": v(645.08, 240) * mm, "end": v(644.66, 242) * mm});
            skLineSegment(sketch, "E359", {"start": v(645.58, 237.6) * mm, "end": v(644.66, 238) * mm});
            skLineSegment(sketch, "E360", {"start": v(645.58, 234.5) * mm, "end": v(645.58, 237.6) * mm});
            skLineSegment(sketch, "E361", {"start": v(642.47, 234.5) * mm, "end": v(645.58, 234.5) * mm});
            skLineSegment(sketch, "E362", {"start": v(642.08, 235.42) * mm, "end": v(642.47, 234.5) * mm});
            skArc(sketch, "E363", {"start": v(638.08, 235.42) * mm, "mid": v(640.08, 235) * mm, "end": v(642.08, 235.42) * mm});
            skLineSegment(sketch, "E364", {"start": v(637.68, 234.5) * mm, "end": v(638.08, 235.42) * mm});
            skLineSegment(sketch, "E365", {"start": v(634.58, 234.5) * mm, "end": v(637.68, 234.5) * mm});
            skLineSegment(sketch, "E366", {"start": v(634.58, 237.6) * mm, "end": v(634.58, 234.5) * mm});
            skLineSegment(sketch, "E367", {"start": v(635.5, 238) * mm, "end": v(634.58, 237.6) * mm});
            skArc(sketch, "E368", {"start": v(635.5, 242) * mm, "mid": v(635.08, 240) * mm, "end": v(635.5, 238) * mm});
            skLineSegment(sketch, "E369", {"start": v(634.58, 242.4) * mm, "end": v(635.5, 242) * mm});
            skLineSegment(sketch, "E370", {"start": v(634.58, 245.5) * mm, "end": v(634.58, 242.4) * mm});
            skLineSegment(sketch, "E371", {"start": v(637.68, 245.5) * mm, "end": v(634.58, 245.5) * mm});
            skLineSegment(sketch, "E372", {"start": v(621.58, 230.5) * mm, "end": v(621.58, 225.5) * mm});
            skArc(sketch, "E373", {"start": v(624.58, 230.5) * mm, "mid": v(623.08, 232) * mm, "end": v(621.58, 230.5) * mm});
            skLineSegment(sketch, "E374", {"start": v(624.58, 228.25) * mm, "end": v(624.58, 230.5) * mm});
            skLineSegment(sketch, "E375", {"start": v(625.58, 228.25) * mm, "end": v(624.58, 228.25) * mm});
            skArc(sketch, "E376", {"start": v(628.33, 225.5) * mm, "mid": v(627.52, 227.44) * mm, "end": v(625.58, 228.25) * mm});
            skLineSegment(sketch, "E377", {"start": v(628.33, 224.5) * mm, "end": v(628.33, 225.5) * mm});
            skLineSegment(sketch, "E378", {"start": v(630.58, 224.5) * mm, "end": v(628.33, 224.5) * mm});
            skArc(sketch, "E379", {"start": v(630.58, 221.5) * mm, "mid": v(632.08, 223) * mm, "end": v(630.58, 224.5) * mm});
            skLineSegment(sketch, "E380", {"start": v(625.58, 221.5) * mm, "end": v(630.58, 221.5) * mm});
            skLineSegment(sketch, "E381", {"start": v(625.58, 222.75) * mm, "end": v(625.58, 221.5) * mm});
            skArc(sketch, "E382", {"start": v(622.83, 225.5) * mm, "mid": v(623.63, 223.56) * mm, "end": v(625.58, 222.75) * mm});
            skLineSegment(sketch, "E383", {"start": v(621.58, 225.5) * mm, "end": v(622.83, 225.5) * mm});
            skLineSegment(sketch, "E384", {"start": v(628.33, 254.5) * mm, "end": v(628.33, 255.5) * mm});
            skArc(sketch, "E385", {"start": v(625.58, 251.75) * mm, "mid": v(627.52, 252.56) * mm, "end": v(628.33, 254.5) * mm});
            skLineSegment(sketch, "E386", {"start": v(624.58, 251.75) * mm, "end": v(625.58, 251.75) * mm});
            skLineSegment(sketch, "E387", {"start": v(624.58, 249.5) * mm, "end": v(624.58, 251.75) * mm});
            skArc(sketch, "E388", {"start": v(621.58, 249.5) * mm, "mid": v(623.08, 248) * mm, "end": v(624.58, 249.5) * mm});
            skLineSegment(sketch, "E389", {"start": v(621.58, 254.5) * mm, "end": v(621.58, 249.5) * mm});
            skLineSegment(sketch, "E390", {"start": v(622.83, 254.5) * mm, "end": v(621.58, 254.5) * mm});
            skArc(sketch, "E391", {"start": v(625.58, 257.25) * mm, "mid": v(623.63, 256.44) * mm, "end": v(622.83, 254.5) * mm});
            skLineSegment(sketch, "E392", {"start": v(625.58, 258.5) * mm, "end": v(625.58, 257.25) * mm});
            skLineSegment(sketch, "E393", {"start": v(630.58, 258.5) * mm, "end": v(625.58, 258.5) * mm});
            skArc(sketch, "E394", {"start": v(630.58, 255.5) * mm, "mid": v(632.08, 257) * mm, "end": v(630.58, 258.5) * mm});
            skLineSegment(sketch, "E395", {"start": v(628.33, 255.5) * mm, "end": v(630.58, 255.5) * mm});
            skLineSegment(sketch, "E396", {"start": v(3.8, 221.5) * mm, "end": v(3.8, 220) * mm});
            skLineSegment(sketch, "E397", {"start": v(3.8, 220) * mm, "end": v(15, 220) * mm});
            skArc(sketch, "E398", {"start": v(15, 220) * mm, "mid": v(17.12, 220.88) * mm, "end": v(18, 223) * mm});
            skLineSegment(sketch, "E399", {"start": v(18, 223) * mm, "end": v(18, 234.2) * mm});
            skLineSegment(sketch, "E400", {"start": v(18, 234.2) * mm, "end": v(16.5, 234.2) * mm});
            skLineSegment(sketch, "E401", {"start": v(16.5, 234.2) * mm, "end": v(16.5, 235) * mm});
            skLineSegment(sketch, "E402", {"start": v(16.5, 235) * mm, "end": v(12, 235) * mm});
            skLineSegment(sketch, "E403", {"start": v(12, 235) * mm, "end": v(12, 229.95) * mm});
            skLineSegment(sketch, "E404", {"start": v(12, 229.95) * mm, "end": v(9.47, 229.95) * mm});
            skLineSegment(sketch, "E405", {"start": v(9.47, 229.95) * mm, "end": v(5.5, 233.91) * mm});
            skLineSegment(sketch, "E406", {"start": v(5.5, 233.91) * mm, "end": v(5.5, 246.09) * mm});
            skLineSegment(sketch, "E407", {"start": v(5.5, 246.09) * mm, "end": v(9.47, 250.05) * mm});
            skLineSegment(sketch, "E408", {"start": v(9.47, 250.05) * mm, "end": v(12, 250.05) * mm});
            skLineSegment(sketch, "E409", {"start": v(12, 250.05) * mm, "end": v(12, 245) * mm});
            skLineSegment(sketch, "E410", {"start": v(12, 245) * mm, "end": v(16.5, 245) * mm});
            skLineSegment(sketch, "E411", {"start": v(16.5, 245) * mm, "end": v(16.5, 245.8) * mm});
            skLineSegment(sketch, "E412", {"start": v(16.5, 245.8) * mm, "end": v(18, 245.8) * mm});
            skLineSegment(sketch, "E413", {"start": v(18, 245.8) * mm, "end": v(18, 257) * mm});
            skArc(sketch, "E414", {"start": v(18, 257) * mm, "mid": v(17.12, 259.12) * mm, "end": v(15, 260) * mm});
            skLineSegment(sketch, "E415", {"start": v(15, 260) * mm, "end": v(3.8, 260) * mm});
            skLineSegment(sketch, "E416", {"start": v(3.8, 260) * mm, "end": v(3.8, 258.5) * mm});
            skLineSegment(sketch, "E417", {"start": v(3.8, 258.5) * mm, "end": v(3, 258.5) * mm});
            skLineSegment(sketch, "E418", {"start": v(3, 258.5) * mm, "end": v(3, 254) * mm});
            skLineSegment(sketch, "E419", {"start": v(3, 254) * mm, "end": v(8.05, 254) * mm});
            skLineSegment(sketch, "E420", {"start": v(8.05, 254) * mm, "end": v(8.05, 251.46) * mm});
            skLineSegment(sketch, "E421", {"start": v(8.05, 251.46) * mm, "end": v(4.09, 247.5) * mm});
            skLineSegment(sketch, "E422", {"start": v(4.09, 247.5) * mm, "end": v(-8.08, 247.5) * mm});
            skLineSegment(sketch, "E423", {"start": v(-8.08, 247.5) * mm, "end": v(-12.05, 251.46) * mm});
            skLineSegment(sketch, "E424", {"start": v(-12.05, 251.46) * mm, "end": v(-12.05, 254) * mm});
            skLineSegment(sketch, "E425", {"start": v(-12.05, 254) * mm, "end": v(-7, 254) * mm});
            skLineSegment(sketch, "E426", {"start": v(-7, 254) * mm, "end": v(-7, 258.5) * mm});
            skLineSegment(sketch, "E427", {"start": v(-7, 258.5) * mm, "end": v(-7.8, 258.5) * mm});
            skLineSegment(sketch, "E428", {"start": v(-7.8, 258.5) * mm, "end": v(-7.8, 260) * mm});
            skLineSegment(sketch, "E429", {"start": v(-7.8, 260) * mm, "end": v(-19, 260) * mm});
            skArc(sketch, "E430", {"start": v(-19, 260) * mm, "mid": v(-21.12, 259.12) * mm, "end": v(-22, 257) * mm});
            skLineSegment(sketch, "E431", {"start": v(-22, 257) * mm, "end": v(-22, 245.8) * mm});
            skLineSegment(sketch, "E432", {"start": v(-22, 245.8) * mm, "end": v(-20.5, 245.8) * mm});
            skLineSegment(sketch, "E433", {"start": v(-20.5, 245.8) * mm, "end": v(-20.5, 245) * mm});
            skLineSegment(sketch, "E434", {"start": v(-20.5, 245) * mm, "end": v(-16, 245) * mm});
            skLineSegment(sketch, "E435", {"start": v(-16, 245) * mm, "end": v(-16, 250.05) * mm});
            skLineSegment(sketch, "E436", {"start": v(-16, 250.05) * mm, "end": v(-13.46, 250.05) * mm});
            skLineSegment(sketch, "E437", {"start": v(-13.46, 250.05) * mm, "end": v(-9.5, 246.09) * mm});
            skLineSegment(sketch, "E438", {"start": v(-9.5, 246.09) * mm, "end": v(-9.5, 233.91) * mm});
            skLineSegment(sketch, "E439", {"start": v(-9.5, 233.91) * mm, "end": v(-13.46, 229.95) * mm});
            skLineSegment(sketch, "E440", {"start": v(-13.46, 229.95) * mm, "end": v(-16, 229.95) * mm});
            skLineSegment(sketch, "E441", {"start": v(-16, 229.95) * mm, "end": v(-16, 235) * mm});
            skLineSegment(sketch, "E442", {"start": v(-16, 235) * mm, "end": v(-20.5, 235) * mm});
            skLineSegment(sketch, "E443", {"start": v(-20.5, 235) * mm, "end": v(-20.5, 234.2) * mm});
            skLineSegment(sketch, "E444", {"start": v(-20.5, 234.2) * mm, "end": v(-22, 234.2) * mm});
            skLineSegment(sketch, "E445", {"start": v(-22, 234.2) * mm, "end": v(-22, 223) * mm});
            skArc(sketch, "E446", {"start": v(-22, 223) * mm, "mid": v(-21.12, 220.88) * mm, "end": v(-19, 220) * mm});
            skLineSegment(sketch, "E447", {"start": v(-19, 220) * mm, "end": v(-7.8, 220) * mm});
            skLineSegment(sketch, "E448", {"start": v(-7.8, 220) * mm, "end": v(-7.8, 221.5) * mm});
            skLineSegment(sketch, "E449", {"start": v(-7.8, 221.5) * mm, "end": v(-7, 221.5) * mm});
            skLineSegment(sketch, "E450", {"start": v(-7, 221.5) * mm, "end": v(-7, 226) * mm});
            skLineSegment(sketch, "E451", {"start": v(-7, 226) * mm, "end": v(-12.05, 226) * mm});
            skLineSegment(sketch, "E452", {"start": v(-12.05, 226) * mm, "end": v(-12.05, 228.54) * mm});
            skLineSegment(sketch, "E453", {"start": v(-12.05, 228.54) * mm, "end": v(-8.08, 232.5) * mm});
            skLineSegment(sketch, "E454", {"start": v(-8.08, 232.5) * mm, "end": v(4.09, 232.5) * mm});
            skLineSegment(sketch, "E455", {"start": v(4.09, 232.5) * mm, "end": v(8.05, 228.54) * mm});
            skLineSegment(sketch, "E456", {"start": v(8.05, 228.54) * mm, "end": v(8.05, 226) * mm});
            skLineSegment(sketch, "E457", {"start": v(8.05, 226) * mm, "end": v(3, 226) * mm});
            skLineSegment(sketch, "E458", {"start": v(3, 226) * mm, "end": v(3, 221.5) * mm});
            skLineSegment(sketch, "E459", {"start": v(3, 221.5) * mm, "end": v(3.8, 221.5) * mm});
            skLineSegment(sketch, "E460", {"start": v(16.5, 249.5) * mm, "end": v(16.5, 254.5) * mm});
            skArc(sketch, "E461", {"start": v(13.5, 249.5) * mm, "mid": v(15, 248) * mm, "end": v(16.5, 249.5) * mm});
            skLineSegment(sketch, "E462", {"start": v(13.5, 251.75) * mm, "end": v(13.5, 249.5) * mm});
            skLineSegment(sketch, "E463", {"start": v(12.5, 251.75) * mm, "end": v(13.5, 251.75) * mm});
            skArc(sketch, "E464", {"start": v(9.75, 254.5) * mm, "mid": v(10.56, 252.56) * mm, "end": v(12.5, 251.75) * mm});
            skLineSegment(sketch, "E465", {"start": v(9.75, 255.5) * mm, "end": v(9.75, 254.5) * mm});
            skLineSegment(sketch, "E466", {"start": v(7.5, 255.5) * mm, "end": v(9.75, 255.5) * mm});
            skArc(sketch, "E467", {"start": v(7.5, 258.5) * mm, "mid": v(6, 257) * mm, "end": v(7.5, 255.5) * mm});
            skLineSegment(sketch, "E468", {"start": v(12.5, 258.5) * mm, "end": v(7.5, 258.5) * mm});
            skLineSegment(sketch, "E469", {"start": v(12.5, 257.25) * mm, "end": v(12.5, 258.5) * mm});
            skArc(sketch, "E470", {"start": v(15.25, 254.5) * mm, "mid": v(14.45, 256.44) * mm, "end": v(12.5, 257.25) * mm});
            skLineSegment(sketch, "E471", {"start": v(16.5, 254.5) * mm, "end": v(15.25, 254.5) * mm});
            skLineSegment(sketch, "E472", {"start": v(9.75, 225.5) * mm, "end": v(9.75, 224.5) * mm});
            skArc(sketch, "E473", {"start": v(12.5, 228.25) * mm, "mid": v(10.56, 227.44) * mm, "end": v(9.75, 225.5) * mm});
            skLineSegment(sketch, "E474", {"start": v(13.5, 228.25) * mm, "end": v(12.5, 228.25) * mm});
            skLineSegment(sketch, "E475", {"start": v(13.5, 230.5) * mm, "end": v(13.5, 228.25) * mm});
            skArc(sketch, "E476", {"start": v(16.5, 230.5) * mm, "mid": v(15, 232) * mm, "end": v(13.5, 230.5) * mm});
            skLineSegment(sketch, "E477", {"start": v(16.5, 225.5) * mm, "end": v(16.5, 230.5) * mm});
            skLineSegment(sketch, "E478", {"start": v(15.25, 225.5) * mm, "end": v(16.5, 225.5) * mm});
            skArc(sketch, "E479", {"start": v(12.5, 222.75) * mm, "mid": v(14.45, 223.56) * mm, "end": v(15.25, 225.5) * mm});
            skLineSegment(sketch, "E480", {"start": v(12.5, 221.5) * mm, "end": v(12.5, 222.75) * mm});
            skLineSegment(sketch, "E481", {"start": v(7.5, 221.5) * mm, "end": v(12.5, 221.5) * mm});
            skArc(sketch, "E482", {"start": v(7.5, 224.5) * mm, "mid": v(6, 223) * mm, "end": v(7.5, 221.5) * mm});
            skLineSegment(sketch, "E483", {"start": v(9.75, 224.5) * mm, "end": v(7.5, 224.5) * mm});
            skLineSegment(sketch, "E484", {"start": v(-4, 244.58) * mm, "end": v(-4.4, 245.5) * mm});
            skArc(sketch, "E485", {"start": v(0, 244.58) * mm, "mid": v(-2, 245) * mm, "end": v(-4, 244.58) * mm});
            skLineSegment(sketch, "E486", {"start": v(0.4, 245.5) * mm, "end": v(0, 244.58) * mm});
            skLineSegment(sketch, "E487", {"start": v(3.5, 245.5) * mm, "end": v(0.4, 245.5) * mm});
            skLineSegment(sketch, "E488", {"start": v(3.5, 242.4) * mm, "end": v(3.5, 245.5) * mm});
            skLineSegment(sketch, "E489", {"start": v(2.58, 242) * mm, "end": v(3.5, 242.4) * mm});
            skArc(sketch, "E490", {"start": v(2.58, 238) * mm, "mid": v(3, 240) * mm, "end": v(2.58, 242) * mm});
            skLineSegment(sketch, "E491", {"start": v(3.5, 237.6) * mm, "end": v(2.58, 238) * mm});
            skLineSegment(sketch, "E492", {"start": v(3.5, 234.5) * mm, "end": v(3.5, 237.6) * mm});
            skLineSegment(sketch, "E493", {"start": v(0.4, 234.5) * mm, "end": v(3.5, 234.5) * mm});
            skLineSegment(sketch, "E494", {"start": v(0, 235.42) * mm, "end": v(0.4, 234.5) * mm});
            skArc(sketch, "E495", {"start": v(-4, 235.42) * mm, "mid": v(-2, 235) * mm, "end": v(0, 235.42) * mm});
            skLineSegment(sketch, "E496", {"start": v(-4.4, 234.5) * mm, "end": v(-4, 235.42) * mm});
            skLineSegment(sketch, "E497", {"start": v(-7.5, 234.5) * mm, "end": v(-4.4, 234.5) * mm});
            skLineSegment(sketch, "E498", {"start": v(-7.5, 237.6) * mm, "end": v(-7.5, 234.5) * mm});
            skLineSegment(sketch, "E499", {"start": v(-6.58, 238) * mm, "end": v(-7.5, 237.6) * mm});
            skArc(sketch, "E500", {"start": v(-6.58, 242) * mm, "mid": v(-7, 240) * mm, "end": v(-6.58, 238) * mm});
            skLineSegment(sketch, "E501", {"start": v(-7.5, 242.4) * mm, "end": v(-6.58, 242) * mm});
            skLineSegment(sketch, "E502", {"start": v(-7.5, 245.5) * mm, "end": v(-7.5, 242.4) * mm});
            skLineSegment(sketch, "E503", {"start": v(-4.4, 245.5) * mm, "end": v(-7.5, 245.5) * mm});
            skLineSegment(sketch, "E504", {"start": v(-20.5, 230.5) * mm, "end": v(-20.5, 225.5) * mm});
            skArc(sketch, "E505", {"start": v(-17.5, 230.5) * mm, "mid": v(-19, 232) * mm, "end": v(-20.5, 230.5) * mm});
            skLineSegment(sketch, "E506", {"start": v(-17.5, 228.25) * mm, "end": v(-17.5, 230.5) * mm});
            skLineSegment(sketch, "E507", {"start": v(-16.5, 228.25) * mm, "end": v(-17.5, 228.25) * mm});
            skArc(sketch, "E508", {"start": v(-13.75, 225.5) * mm, "mid": v(-14.55, 227.44) * mm, "end": v(-16.5, 228.25) * mm});
            skLineSegment(sketch, "E509", {"start": v(-13.75, 224.5) * mm, "end": v(-13.75, 225.5) * mm});
            skLineSegment(sketch, "E510", {"start": v(-11.5, 224.5) * mm, "end": v(-13.75, 224.5) * mm});
            skArc(sketch, "E511", {"start": v(-11.5, 221.5) * mm, "mid": v(-10, 223) * mm, "end": v(-11.5, 224.5) * mm});
            skLineSegment(sketch, "E512", {"start": v(-16.5, 221.5) * mm, "end": v(-11.5, 221.5) * mm});
            skLineSegment(sketch, "E513", {"start": v(-16.5, 222.75) * mm, "end": v(-16.5, 221.5) * mm});
            skArc(sketch, "E514", {"start": v(-19.25, 225.5) * mm, "mid": v(-18.44, 223.56) * mm, "end": v(-16.5, 222.75) * mm});
            skLineSegment(sketch, "E515", {"start": v(-20.5, 225.5) * mm, "end": v(-19.25, 225.5) * mm});
            skLineSegment(sketch, "E516", {"start": v(-13.75, 254.5) * mm, "end": v(-13.75, 255.5) * mm});
            skArc(sketch, "E517", {"start": v(-16.5, 251.75) * mm, "mid": v(-14.55, 252.56) * mm, "end": v(-13.75, 254.5) * mm});
            skLineSegment(sketch, "E518", {"start": v(-17.5, 251.75) * mm, "end": v(-16.5, 251.75) * mm});
            skLineSegment(sketch, "E519", {"start": v(-17.5, 249.5) * mm, "end": v(-17.5, 251.75) * mm});
            skArc(sketch, "E520", {"start": v(-20.5, 249.5) * mm, "mid": v(-19, 248) * mm, "end": v(-17.5, 249.5) * mm});
            skLineSegment(sketch, "E521", {"start": v(-20.5, 254.5) * mm, "end": v(-20.5, 249.5) * mm});
            skLineSegment(sketch, "E522", {"start": v(-19.25, 254.5) * mm, "end": v(-20.5, 254.5) * mm});
            skArc(sketch, "E523", {"start": v(-16.5, 257.25) * mm, "mid": v(-18.44, 256.44) * mm, "end": v(-19.25, 254.5) * mm});
            skLineSegment(sketch, "E524", {"start": v(-16.5, 258.5) * mm, "end": v(-16.5, 257.25) * mm});
            skLineSegment(sketch, "E525", {"start": v(-11.5, 258.5) * mm, "end": v(-16.5, 258.5) * mm});
            skArc(sketch, "E526", {"start": v(-11.5, 255.5) * mm, "mid": v(-10, 257) * mm, "end": v(-11.5, 258.5) * mm});
            skLineSegment(sketch, "E527", {"start": v(-13.75, 255.5) * mm, "end": v(-11.5, 255.5) * mm});
            skSolve(sketch);
        }
        {
            var Q0;
            Q0=makeQuery(id+"F0.imprint","IMPRINT",FACE,{"disambiguationData":[TD([[makeQuery(id+"F0.imprint","IMPRINT",EDGE,{"derivedFrom":sQuery(id+"F0.wireOp",EDGE,"E264")}),1.0]])]});
            var Q1;
            Q1=makeQuery(id+"F0.imprint","IMPRINT",FACE,{"disambiguationData":[TD([[makeQuery(id+"F0.imprint","IMPRINT",EDGE,{"derivedFrom":sQuery(id+"F0.wireOp",EDGE,"E396")}),1.0]])]});
            var Q2;
            Q2=makeQuery(id+"F0.imprint","IMPRINT",FACE,{"disambiguationData":[TD([[makeQuery(id+"F0.imprint","IMPRINT",EDGE,{"derivedFrom":sQuery(id+"F0.wireOp",EDGE,"E504")}),1.0]])]});
            var Q3;
            Q3=makeQuery(id+"F0.imprint","IMPRINT",FACE,{"disambiguationData":[TD([[makeQuery(id+"F0.imprint","IMPRINT",EDGE,{"derivedFrom":sQuery(id+"F0.wireOp",EDGE,"E340")}),1.0]])]});
            var Q4;
            Q4=makeQuery(id+"F0.imprint","IMPRINT",FACE,{"disambiguationData":[TD([[makeQuery(id+"F0.imprint","IMPRINT",EDGE,{"derivedFrom":sQuery(id+"F0.wireOp",EDGE,"E372")}),1.0]])]});
            var Q5;
            Q5=makeQuery(id+"F0.imprint","IMPRINT",FACE,{"disambiguationData":[TD([[makeQuery(id+"F0.imprint","IMPRINT",EDGE,{"derivedFrom":sQuery(id+"F0.wireOp",EDGE,"E484")}),1.0]])]});
            var Q6;
            Q6=makeQuery(id+"F0.imprint","IMPRINT",FACE,{"disambiguationData":[TD([[makeQuery(id+"F0.imprint","IMPRINT",EDGE,{"derivedFrom":sQuery(id+"F0.wireOp",EDGE,"E516")}),1.0]])]});
            var Q7;
            Q7=makeQuery(id+"F0.imprint","IMPRINT",FACE,{"disambiguationData":[TD([[makeQuery(id+"F0.imprint","IMPRINT",EDGE,{"derivedFrom":sQuery(id+"F0.wireOp",EDGE,"E460")}),1.0]])]});
            var Q8;
            Q8=makeQuery(id+"F0.imprint","IMPRINT",FACE,{"disambiguationData":[TD([[makeQuery(id+"F0.imprint","IMPRINT",EDGE,{"derivedFrom":sQuery(id+"F0.wireOp",EDGE,"E472")}),1.0]])]});
            var Q9;
            Q9=makeQuery(id+"F0.imprint","IMPRINT",FACE,{"disambiguationData":[TD([[makeQuery(id+"F0.imprint","IMPRINT",EDGE,{"derivedFrom":sQuery(id+"F0.wireOp",EDGE,"E352")}),1.0]])]});
            var Q10;
            Q10=makeQuery(id+"F0.imprint","IMPRINT",FACE,{"disambiguationData":[TD([[makeQuery(id+"F0.imprint","IMPRINT",EDGE,{"derivedFrom":sQuery(id+"F0.wireOp",EDGE,"E328")}),1.0]])]});
            var Q11;
            Q11=makeQuery(id+"F0.imprint","IMPRINT",FACE,{"disambiguationData":[TD([[makeQuery(id+"F0.imprint","IMPRINT",EDGE,{"derivedFrom":sQuery(id+"F0.wireOp",EDGE,"E384")}),1.0]])]});
            extrude(context, id + "F1", {"entities" : qUnion([Q0, Q1, Q2, Q3, Q4, Q5, Q6, Q7, Q8, Q9, Q10, Q11]), "depth" : 1000 * mm, "offsetDistance" : 25 * mm});
        }
        {
            var Q0;
            Q0=makeQuery(id+"F0.imprint","IMPRINT",FACE,{"disambiguationData":[TD([[makeQuery(id+"F0.imprint","IMPRINT",EDGE,{"derivedFrom":sQuery(id+"F0.wireOp",EDGE,"E0")}),1.0]])]});
            var Q1;
            Q1=makeQuery(id+"F0.imprint","IMPRINT",FACE,{"disambiguationData":[TD([[makeQuery(id+"F0.imprint","IMPRINT",EDGE,{"derivedFrom":sQuery(id+"F0.wireOp",EDGE,"E132")}),1.0]])]});
            var Q2;
            Q2=makeQuery(id+"F0.imprint","IMPRINT",FACE,{"disambiguationData":[TD([[makeQuery(id+"F0.imprint","IMPRINT",EDGE,{"derivedFrom":sQuery(id+"F0.wireOp",EDGE,"E208")}),1.0]])]});
            var Q3;
            Q3=makeQuery(id+"F0.imprint","IMPRINT",FACE,{"disambiguationData":[TD([[makeQuery(id+"F0.imprint","IMPRINT",EDGE,{"derivedFrom":sQuery(id+"F0.wireOp",EDGE,"E240")}),1.0]])]});
            var Q4;
            Q4=makeQuery(id+"F0.imprint","IMPRINT",FACE,{"disambiguationData":[TD([[makeQuery(id+"F0.imprint","IMPRINT",EDGE,{"derivedFrom":sQuery(id+"F0.wireOp",EDGE,"E252")}),1.0]])]});
            var Q5;
            Q5=makeQuery(id+"F0.imprint","IMPRINT",FACE,{"disambiguationData":[TD([[makeQuery(id+"F0.imprint","IMPRINT",EDGE,{"derivedFrom":sQuery(id+"F0.wireOp",EDGE,"E108")}),1.0]])]});
            var Q6;
            Q6=makeQuery(id+"F0.imprint","IMPRINT",FACE,{"disambiguationData":[TD([[makeQuery(id+"F0.imprint","IMPRINT",EDGE,{"derivedFrom":sQuery(id+"F0.wireOp",EDGE,"E88")}),1.0]])]});
            var Q7;
            Q7=makeQuery(id+"F0.imprint","IMPRINT",FACE,{"disambiguationData":[TD([[makeQuery(id+"F0.imprint","IMPRINT",EDGE,{"derivedFrom":sQuery(id+"F0.wireOp",EDGE,"E196")}),1.0]])]});
            var Q8;
            Q8=makeQuery(id+"F0.imprint","IMPRINT",FACE,{"disambiguationData":[TD([[makeQuery(id+"F0.imprint","IMPRINT",EDGE,{"derivedFrom":sQuery(id+"F0.wireOp",EDGE,"E220")}),1.0]])]});
            var Q9;
            Q9=makeQuery(id+"F0.imprint","IMPRINT",FACE,{"disambiguationData":[TD([[makeQuery(id+"F0.imprint","IMPRINT",EDGE,{"derivedFrom":sQuery(id+"F0.wireOp",EDGE,"E76")}),1.0]])]});
            var Q10;
            Q10=makeQuery(id+"F0.imprint","IMPRINT",FACE,{"disambiguationData":[TD([[makeQuery(id+"F0.imprint","IMPRINT",EDGE,{"derivedFrom":sQuery(id+"F0.wireOp",EDGE,"E120")}),1.0]])]});
            var Q11;
            Q11=makeQuery(id+"F0.imprint","IMPRINT",FACE,{"disambiguationData":[TD([[makeQuery(id+"F0.imprint","IMPRINT",EDGE,{"derivedFrom":sQuery(id+"F0.wireOp",EDGE,"E64")}),1.0]])]});
            extrude(context, id + "F2", {"entities" : qUnion([Q0, Q1, Q2, Q3, Q4, Q5, Q6, Q7, Q8, Q9, Q10, Q11]), "depth" : 1000 * mm, "offsetDistance" : 25 * mm});
        }
    });
